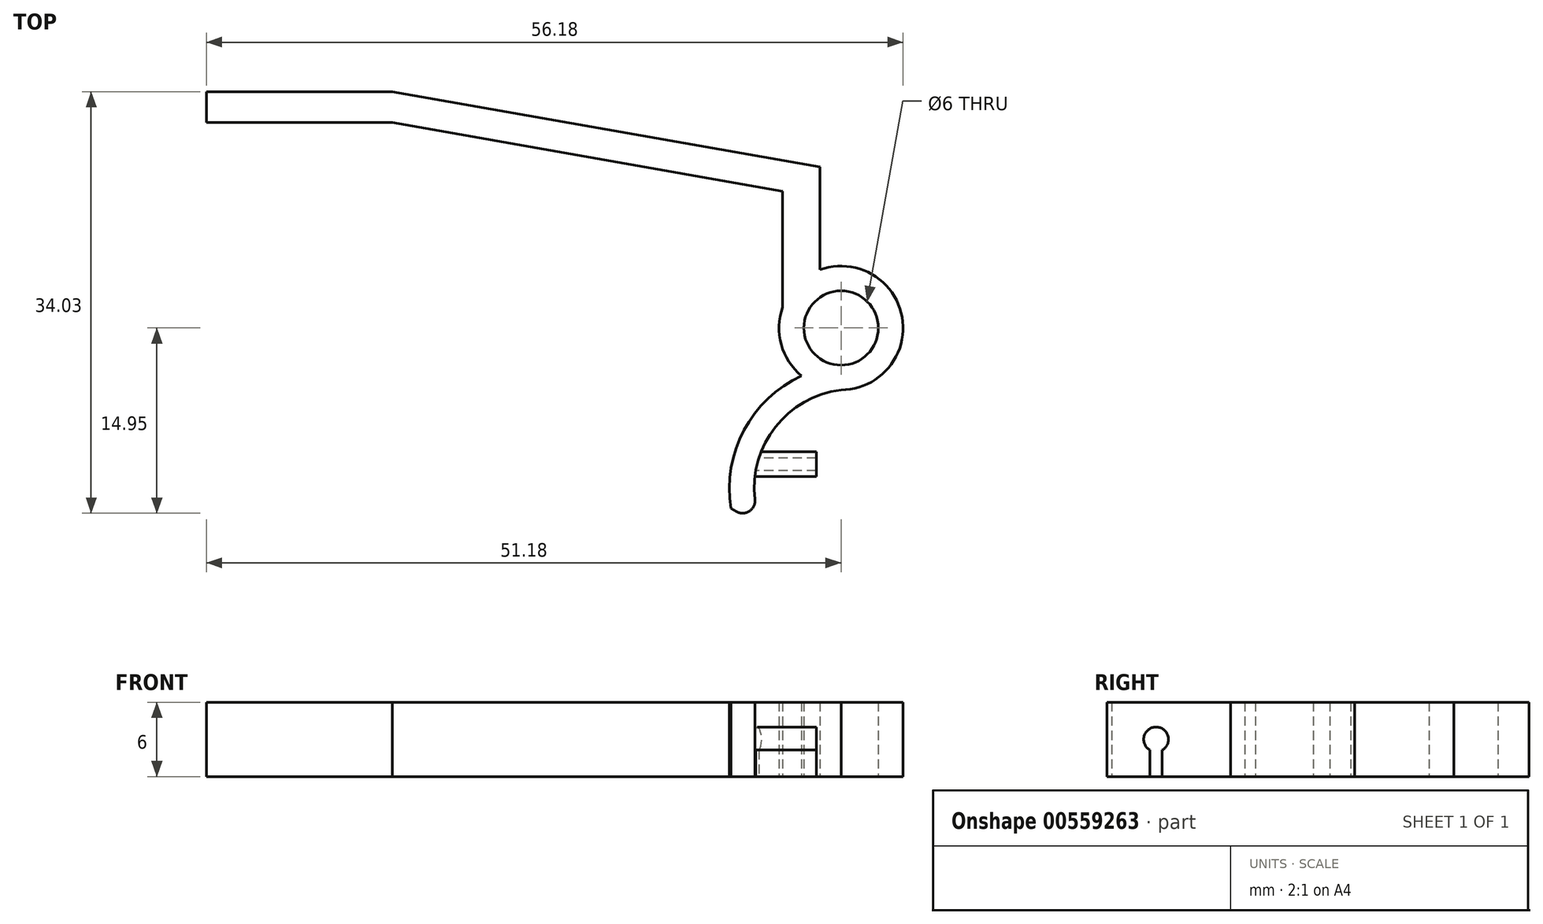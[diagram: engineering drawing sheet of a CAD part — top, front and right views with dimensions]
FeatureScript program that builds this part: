
annotation { "Feature Type Name" : "Feature", "Feature Type Description" : "" }
export const myFeature = defineFeature(function(context is Context, id is Id, definition is map)
    precondition{}
    {
        {
            var Q0;
            Q0=qCreatedBy(makeId("Top.planeOp"),FACE);
            var sketch = newSketch(context, id + "F0", { "sketchPlane" : qUnion([Q0])});
            skCircle(sketch, "E0", {"center": v(0, 0) * mm, "radius": 3 * mm});
            skArc(sketch, "E1", {"start": v(0, -5) * mm, "mid": v(1.7, 4.7) * mm, "end": v(-3.18, -3.85) * mm});
            skArc(sketch, "E2", {"start": v(-3.18, -3.85) * mm, "mid": v(-7.84, -8.25) * mm, "end": v(-8.87, -14.57) * mm});
            skArc(sketch, "E3", {"start": v(0, -5) * mm, "mid": v(-5.29, -8) * mm, "end": v(-6.95, -13.84) * mm});
            skLineSegment(sketch, "E4", {"start": v(-9, 0) * mm, "end": v(-9, -12.1) * mm, "construction": true});
            skLineSegment(sketch, "E5", {"start": v(-8.52, -16) * mm, "end": v(-6.4, -16) * mm, "construction": true});
            skLineSegment(sketch, "E6", {"start": v(-1.71, 4.7) * mm, "end": v(-1.71, 13) * mm});
            skLineSegment(sketch, "E7", {"start": v(-1.71, 13) * mm, "end": v(-36.18, 19.08) * mm});
            skLineSegment(sketch, "E8", {"start": v(-36.18, 19.08) * mm, "end": v(-51.18, 19.08) * mm});
            skLineSegment(sketch, "E9", {"start": v(-51.18, 19.08) * mm, "end": v(-51.18, 16.58) * mm});
            skLineSegment(sketch, "E10", {"start": v(-51.18, 16.58) * mm, "end": v(-36.18, 16.58) * mm});
            skLineSegment(sketch, "E11", {"start": v(-36.18, 16.58) * mm, "end": v(-4.71, 11.03) * mm});
            skLineSegment(sketch, "E12", {"start": v(-4.71, 11.03) * mm, "end": v(-4.71, 1.68) * mm});
            skLineSegment(sketch, "E13", {"start": v(-8.44, -14.82) * mm, "end": v(-8.87, -14.57) * mm});
            skPoint(sketch, "E14.visualSharp", {"position": v(-6.4, -16) * mm});
            skArc(sketch, "E14.filletArc", {"start": v(-8.44, -14.82) * mm, "mid": v(-7.4, -14.79) * mm, "end": v(-6.95, -13.84) * mm});
            skLineSegment(sketch, "E15", {"start": v(0, 0) * mm, "end": v(-1.71, 4.7) * mm, "construction": true});
            skLineSegment(sketch, "E16", {"start": v(0, 0) * mm, "end": v(-19.76, 0) * mm, "construction": true});
            skSolve(sketch);
        }
        {
            var Q0;
            Q0 = qSketchRegion(id + "F0", true);
            extrude(context, id + "F1", {"entities" : qUnion([Q0]), "depth" : 6 * mm, "offsetDistance" : 25 * mm});
        }
        {
            var Q0;
            Q0=qCreatedBy(makeId("Right.planeOp"),FACE);
            cPlane(context, id + "F2", {"entities" : qUnion([Q0]), "cplaneType" : CPlaneType.OFFSET, "offset" : 7 * mm, "oppositeDirection" : true, "width" : 150 * mm, "height" : 150 * mm});
        }
        {
            var Q0;
            Q0=qCreatedBy(id+"F2.planeOp",FACE);
            var sketch = newSketch(context, id + "F3", { "sketchPlane" : qUnion([Q0])});
            skArc(sketch, "E17", {"start": v(-10.5, 2.13) * mm, "mid": v(-11, 4) * mm, "end": v(-11.5, 2.13) * mm});
            skLineSegment(sketch, "E18.bottom", {"start": v(-11.5, 0) * mm, "end": v(-10.5, 0) * mm});
            skLineSegment(sketch, "E18.left", {"start": v(-11.5, 0) * mm, "end": v(-11.5, 2.13) * mm});
            skLineSegment(sketch, "E18.right", {"start": v(-10.5, 0) * mm, "end": v(-10.5, 2.13) * mm});
            skLineSegment(sketch, "E19", {"start": v(-11, 3) * mm, "end": v(-11, 0) * mm, "construction": true});
            skSolve(sketch);
        }
        {
            var Q0;
            Q0 = qSketchRegion(id + "F3", true);
            extrude(context, id + "F4", {"entities" : qUnion([Q0]), "operationType" : NewBodyOperationType.ADD, "depth" : 5 * mm, "offsetDistance" : 25 * mm});
        }
    });
